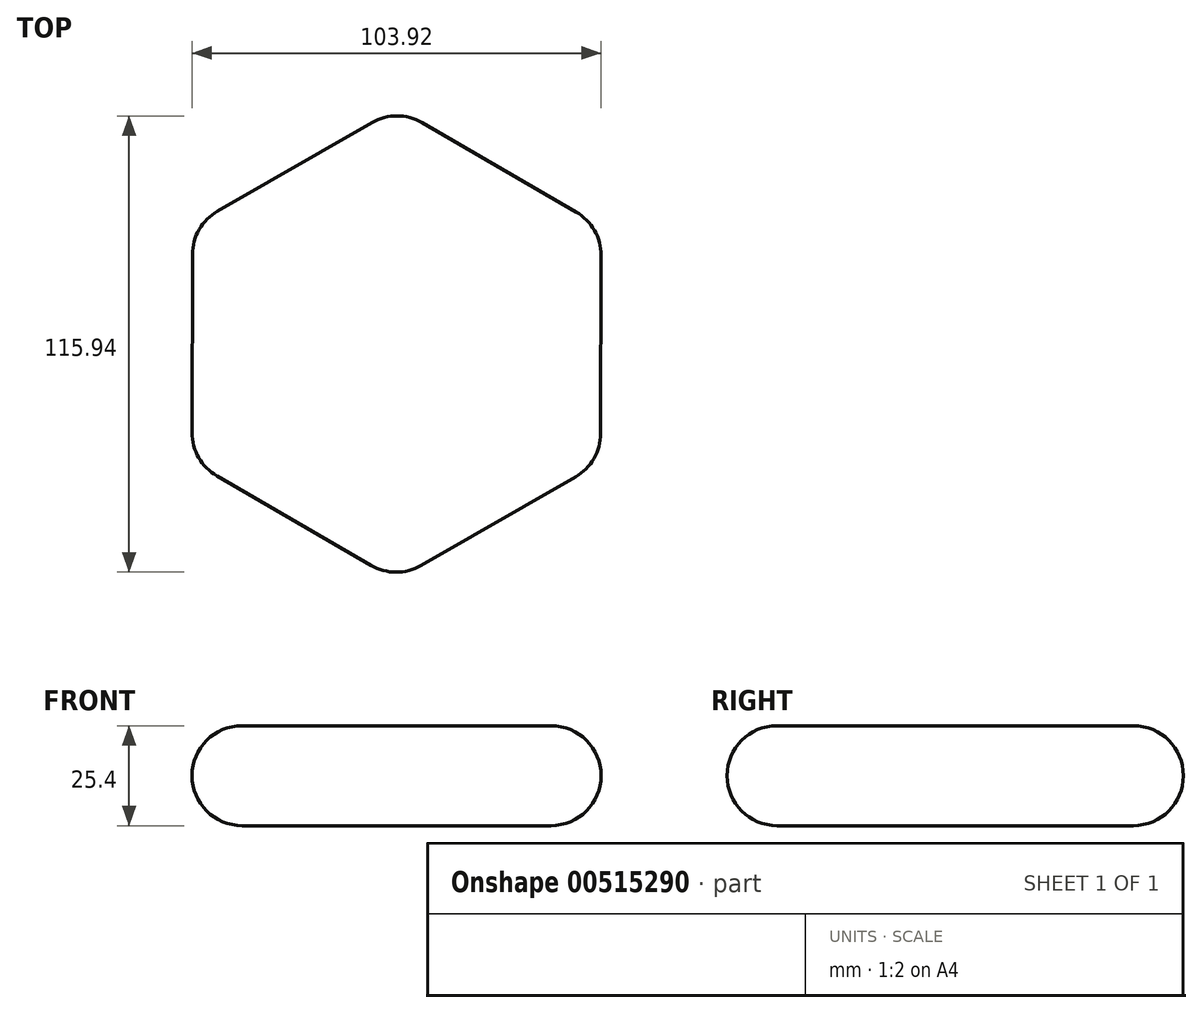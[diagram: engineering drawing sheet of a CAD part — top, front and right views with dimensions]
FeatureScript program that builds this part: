
annotation { "Feature Type Name" : "Feature", "Feature Type Description" : "" }
export const myFeature = defineFeature(function(context is Context, id is Id, definition is map)
    precondition{}
    {
        {
            var Q0;
            Q0=qCreatedBy(makeId("Top.planeOp"),FACE);
            var sketch = newSketch(context, id + "F0", { "sketchPlane" : qUnion([Q0])});
            skCircle(sketch, "E0.cCircle", {"center": v(0, 0) * mm, "radius": 51.9 * mm, "construction": true});
            skLineSegment(sketch, "E0.0", {"start": v(0.14, 59.93) * mm, "end": v(51.97, 29.85) * mm});
            skLineSegment(sketch, "E0.1", {"start": v(51.97, 29.85) * mm, "end": v(51.83, -30.09) * mm});
            skLineSegment(sketch, "E0.2", {"start": v(51.83, -30.09) * mm, "end": v(-0.14, -59.93) * mm});
            skLineSegment(sketch, "E0.3", {"start": v(-0.14, -59.93) * mm, "end": v(-51.97, -29.85) * mm});
            skLineSegment(sketch, "E0.4", {"start": v(-51.97, -29.85) * mm, "end": v(-51.83, 30.09) * mm});
            skLineSegment(sketch, "E0.5", {"start": v(-51.83, 30.09) * mm, "end": v(0.14, 59.93) * mm});
            skPoint(sketch, "E0.0.midPoint", {"position": v(26.05, 44.89) * mm});
            skSolve(sketch);
        }
        {
            var Q0;
            Q0 = qSketchRegion(id + "F0", true);
            extrude(context, id + "F1", {"entities" : qUnion([Q0]), "depth" : 25.4 * mm, "offsetDistance" : 25.4 * mm});
        }
        {
            var Q0;
            Q0=makeQuery(id+"F1.opExtrude","SWEPT_FACE",FACE,{"disambiguationData":[OSD([sQuery(id+"F0.wireOp",EDGE,"E0.0")])]});
            var Q1;
            Q1=makeQuery(id+"F1.opExtrude","SWEPT_FACE",FACE,{"disambiguationData":[OSD([sQuery(id+"F0.wireOp",EDGE,"E0.5")])]});
            var Q2;
            Q2=makeQuery(id+"F1.opExtrude","SWEPT_FACE",FACE,{"disambiguationData":[OSD([sQuery(id+"F0.wireOp",EDGE,"E0.4")])]});
            var Q3;
            Q3=makeQuery(id+"F1.opExtrude","SWEPT_FACE",FACE,{"disambiguationData":[OSD([sQuery(id+"F0.wireOp",EDGE,"E0.2")])]});
            var Q4;
            Q4=makeQuery(id+"F1.opExtrude","SWEPT_FACE",FACE,{"disambiguationData":[OSD([sQuery(id+"F0.wireOp",EDGE,"E0.3")])]});
            var Q5;
            Q5=makeQuery(id+"F1.opExtrude","SWEPT_FACE",FACE,{"disambiguationData":[OSD([sQuery(id+"F0.wireOp",EDGE,"E0.1")])]});
            fillet(context, id + "F2", {"entities" : qUnion([Q0, Q1, Q2, Q3, Q4, Q5]), "radius" : 12.7 * mm, "tangentPropagation" : true, "allowEdgeOverflow" : false});
        }
    });
